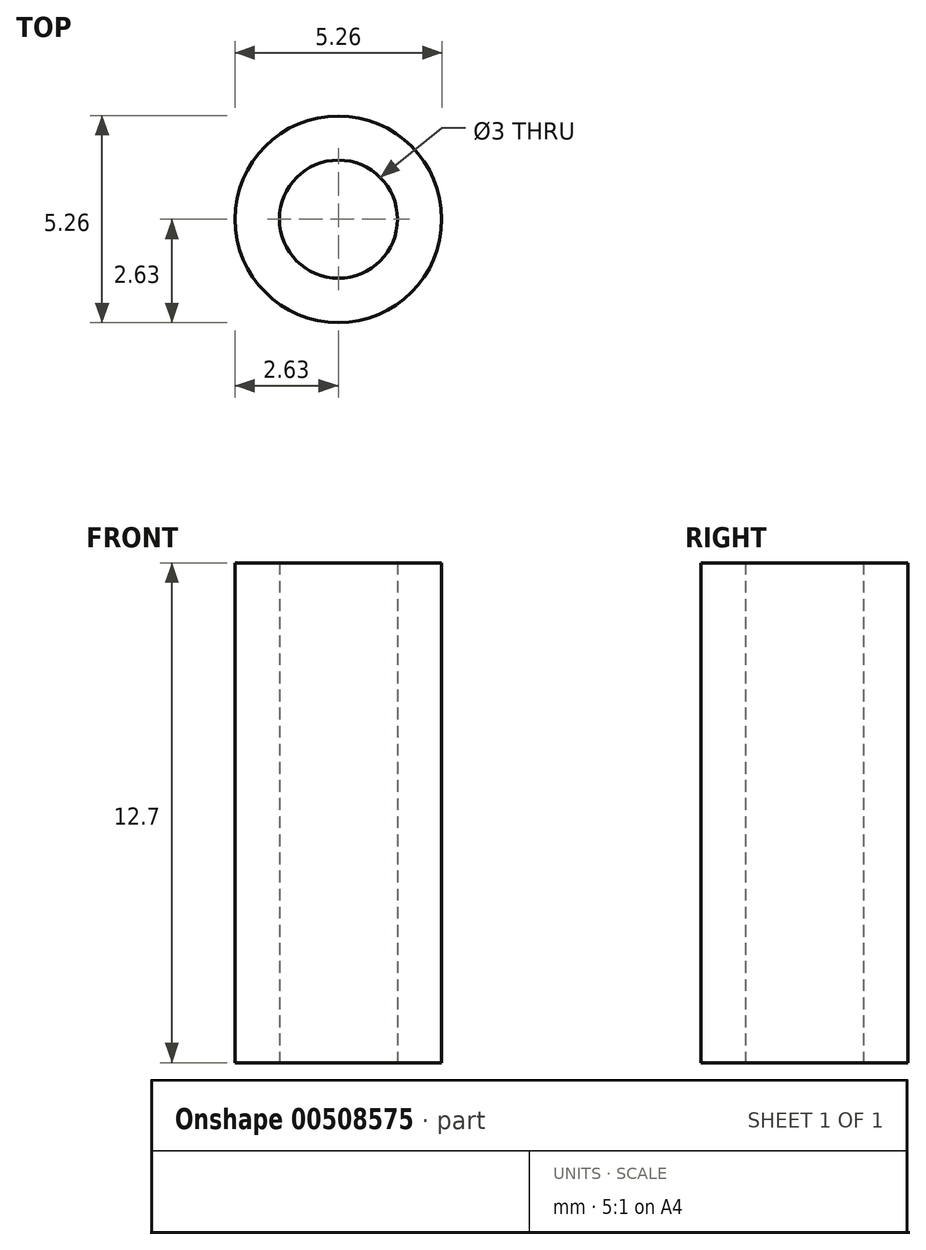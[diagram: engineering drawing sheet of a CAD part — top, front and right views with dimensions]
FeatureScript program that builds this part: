
annotation { "Feature Type Name" : "Feature", "Feature Type Description" : "" }
export const myFeature = defineFeature(function(context is Context, id is Id, definition is map)
    precondition{}
    {
        {
            var Q0;
            Q0=qCreatedBy(makeId("Top.planeOp"), FACE);
            var sketch = newSketch(context, id + "F0", { "sketchPlane" : qUnion([Q0])});
            skCircle(sketch, "E0", {"center": v(0, 0) * mm, "radius": 1.5 * mm});
            skCircle(sketch, "E1", {"center": v(0, 0) * mm, "radius": 2.62 * mm});
            skSolve(sketch);
        }
        {
            var Q0;
            Q0 = qSketchRegion(id + "F0", true);
            extrude(context, id + "F1", {"entities" : qUnion([Q0]), "depth" : (25.4 / 2) * mm, "offsetDistance" : 25 * mm});
        }
    });
